# Revit family: IS_ConnectAir_E1055_BIM_DE
name_source: partatom
category: Plumbing Fixtures
revit_build: Autodesk Revit MEP 2014 (Build: 20130308_1515(x64)
units: mm (PartAtom-declared; Revit-internal decimal feet)

## types (1)
- E105501 - Connect Air pentagon shower tray
    Accessories = www.idealstandard.de\ersatzteile
    AreaUnits = millimeters
    Assembly Code = C1030200
    AssetType = Fixed
    BIMObjectName = ISI_IdealStandard_ShowerTrays_ConnectAir_E105501
    BarCode = 5017830518679
    Brand = Ideal Standard
    CWFU = 0
    Category = SanitaryTerminal_SHOWER
    CodePerformance = DIN EN 14527, DIN EN 251, DIN EN 249
    Color = White
    ConnectionType = Plumbing
    Cost = 0 $
    Default Elevation = 0 mm  [stored 0 ft]
    Description = Connect Air pentagon shower tray
    DrainSize = 90 mm  [stored 0.295276 ft]
    DurationUnit = year
    ExpectedLife = 25
    Features = Connect Air pentagon shower tray
    Finish = white
    HWFU = 0
    HasTray = Yes
    IfcExportAs = IfcSanitaryTerminalType
    IfcExportType = SHOWER
    InstallationInstructions = www.idealstandard.de/produkte
    LinearUnits = millimeters
    ManufacturerURL = www.idealstandard.com
    Material = Acrylic
    MaterialThickness = 0 mm  [stored 0 ft]
    Model = E105501
    ModelNumber = E105501
    ModelReference = Connect Air pentagon shower tray
    NBSDescription = Shower trays
    NBSReference = 45-35-70/336
    Name = ShowerTrays_ConnectAir_E105501_IdealStandard
    NettWeight = 13 kg
    NominalHeight = 40 mm
    NominalLength = 900 mm
    NominalWidth = 900 mm
    ProductInformation = www.idealstandard.de/produkte
    Shape = Rectangular
    Size = 900x900x40mm
    Space = Internal
    SpareParts = www.idealstandard.de/ersatzteile
    TMV3 = No
    URL = www.idealstandard.com
    Uniclass2015Code = Pr_40_20_06_84
    Uniclass2015Title = Shower trays
    Uniclass2015Version = Products v1.1
    Version = 1
    VolumeUnits = Litres
    WarrantyDescription = Manufacturers Warranty
    WarrantyDurationUnit = year

note: [stored X ft] marks values corroborated as IEEE doubles in the binary element streams (Revit-internal decimal feet)

## geometry (parser evidence)
native form markers: Sweep x5
no freeform markers — native parametric forms only
